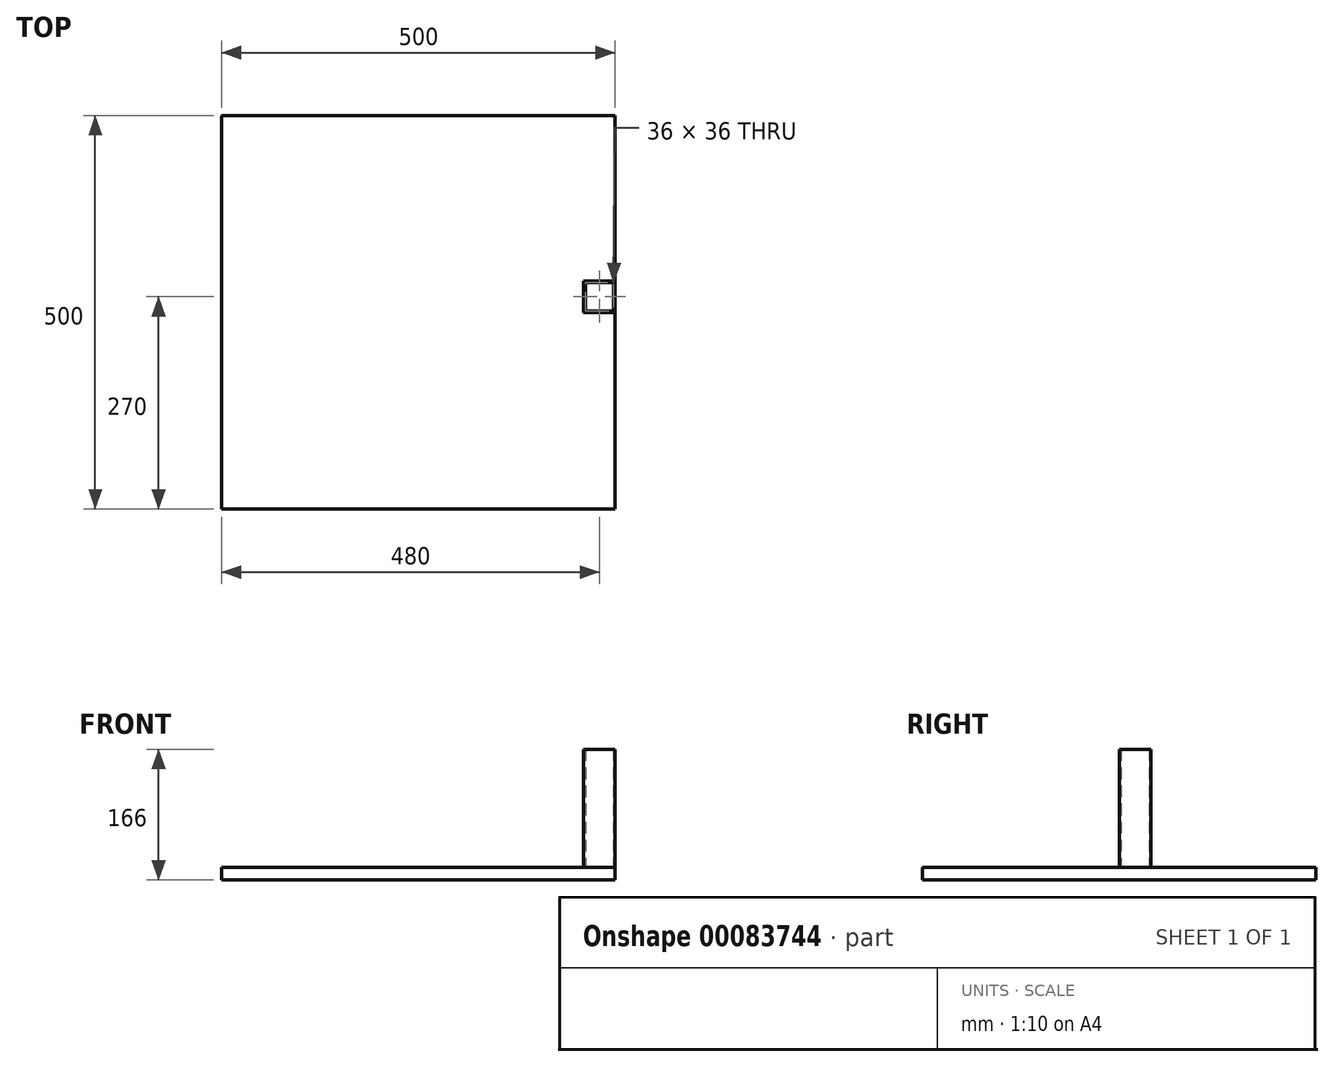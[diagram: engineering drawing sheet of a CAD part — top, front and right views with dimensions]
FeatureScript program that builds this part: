
annotation { "Feature Type Name" : "Feature", "Feature Type Description" : "" }
export const myFeature = defineFeature(function(context is Context, id is Id, definition is map)
    precondition{}
    {
        {
            var Q0;
            Q0=qCreatedBy(makeId("Top.planeOp"),FACE);
            var sketch = newSketch(context, id + "F0", { "sketchPlane" : qUnion([Q0])});
            skLineSegment(sketch, "E0.bottom", {"start": v(-250, 250) * mm, "end": v(250, 250) * mm});
            skLineSegment(sketch, "E0.top", {"start": v(-250, -250) * mm, "end": v(250, -250) * mm});
            skLineSegment(sketch, "E0.left", {"start": v(-250, 250) * mm, "end": v(-250, -250) * mm});
            skLineSegment(sketch, "E0.right", {"start": v(250, 250) * mm, "end": v(250, -250) * mm});
            skLineSegment(sketch, "E1", {"start": v(-250, 250) * mm, "end": v(250, -250) * mm, "construction": true});
            skSolve(sketch);
        }
        {
            var Q0;
            Q0 = qSketchRegion(id + "F0", true);
            extrude(context, id + "F1", {"entities" : qUnion([Q0]), "depth" : 16 * mm});
        }
        {
            var Q0;
            Q0=makeQuery(id+"F1.opExtrude","CAP_FACE",FACE,{"disambiguationData":[OSD([sQuery(id+"F0.wireOp",EDGE,"E0.bottom"),sQuery(id+"F0.wireOp",EDGE,"E0.top"),sQuery(id+"F0.wireOp",EDGE,"E0.left"),sQuery(id+"F0.wireOp",EDGE,"E0.right")])],"isStart":false});
            var sketch = newSketch(context, id + "F2", { "sketchPlane" : qUnion([Q0])});
            skLineSegment(sketch, "E2.bottom", {"start": v(210, 40) * mm, "end": v(250, 40) * mm});
            skLineSegment(sketch, "E2.top", {"start": v(210, 0) * mm, "end": v(250, 0) * mm});
            skLineSegment(sketch, "E2.left", {"start": v(210, 40) * mm, "end": v(210, 0) * mm});
            skLineSegment(sketch, "E2.right", {"start": v(250, 40) * mm, "end": v(250, 0) * mm});
            skLineSegment(sketch, "E3.bottom", {"start": v(212, 38) * mm, "end": v(248, 38) * mm});
            skLineSegment(sketch, "E3.top", {"start": v(212, 2) * mm, "end": v(248, 2) * mm});
            skLineSegment(sketch, "E3.left", {"start": v(212, 38) * mm, "end": v(212, 2) * mm});
            skLineSegment(sketch, "E3.right", {"start": v(248, 38) * mm, "end": v(248, 2) * mm});
            skLineSegment(sketch, "E4", {"start": v(212, 38) * mm, "end": v(248, 2) * mm, "construction": true});
            skLineSegment(sketch, "E5", {"start": v(250, 40) * mm, "end": v(210, 0) * mm, "construction": true});
            skPoint(sketch, "E6", {"position": v(230, 20) * mm});
            skSolve(sketch);
        }
        {
            var Q0;
            Q0 = qSketchRegion(id + "F2", true);
            extrude(context, id + "F3", {"entities" : qUnion([Q0]), "depth" : 150 * mm});
        }
    });
